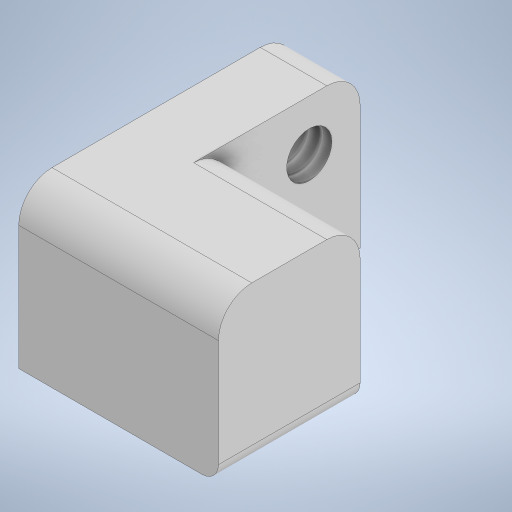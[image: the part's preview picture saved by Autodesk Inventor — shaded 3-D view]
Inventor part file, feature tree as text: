
AUTODESK INVENTOR PART (.ipt)
format: ipt  version: 2024.1 (Build 281209000, 209)  size: 263,680 bytes
history: native  units: in
note: dims shown in document units (in); Inventor stores cm internally (conversion verified against a paired STEP export)
features: sketch x6, extrude x5, projected_geometry x5, fillet x2, hole x1
ambient origin geometry x8: Origin, YZ Plane, XZ Plane, XY Plane, X Axis, Y Axis, Z Axis, Center Point
bodies: Solid1 (feature_tree)
feature tree (19):
  extrude  "Extrusion1"  Depth=0.25in
  hole  "Hole1"  [1 undecoded]
  extrude  "Extrusion2"  Depth=0.125in
  extrude  "Extrusion3"  Depth=0.0295in TaperAngle=0.0deg
  extrude  "Extrusion4"  Depth=0.0312in TaperAngle=0.0deg
  extrude  "Extrusion5"  Depth=0.375in
  fillet  "Fillet1"  Radius=0.0625in
  fillet  "Fillet2"  Radius=0.0295in
  sketch  "Sketch1"  dims[d0=0.125in d1=0.25in]
  sketch  "Sketch2"  dims[d2=0.375in d3=0.325in]
  sketch  "Sketch3"  dims[d4=0.325in d5=0.0in d6=0.125in]
  projected_geometry  "Projected Loop1"
  sketch  "Sketch4"  dims[d7=0.125in]
  projected_geometry  "Projected Loop2"
  sketch  "Sketch5"  dims[d8=0.0849in d9=0.224in d10=0.219in d11=0.112in d12=0.5635in d13=0.349in d14=0.8108in d15=0.0295in d16=0.0in]
  projected_geometry  "Projected Loop3"
  projected_geometry  "Projected Loop4"
  sketch  "Sketch6"  dims[d17=0.0295in d18=0.0in d19=0.0295in d20=0.0in d21=0.375in d22=0.0625in d23=0.0295in d24=0.0in d25=0.0312in]
  projected_geometry  "Projected Loop5"
note: 1 required parameter value undecoded (feature->parameter linkage not recoverable at this tier; creation-order binding heuristic only, values carry confidence <= 0.55)
